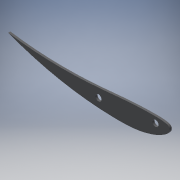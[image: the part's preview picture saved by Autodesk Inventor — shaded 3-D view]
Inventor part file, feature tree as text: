
AUTODESK INVENTOR PART (.ipt)
format: ipt  version: 2018.2 (Build 222227000, 227)  size: 139,264 bytes
history: native  units: mm
features: extrude x2, sketch x2, other x1, projected_geometry x1
ambient origin geometry x8: Origin, YZ Plane, XZ Plane, XY Plane, X Axis, Y Axis, Z Axis, Center Point
bodies: Body1 (feature_tree)
feature tree (6):
  extrude  "押し出し1"  Depth=4.0mm TaperAngle=0.0deg
  extrude  "押し出し2"  Depth=20.0mm
  other  "厚み1"
  sketch  "スケッチ1"
  projected_geometry  "投影ループ1"
  sketch  "スケッチ2"
